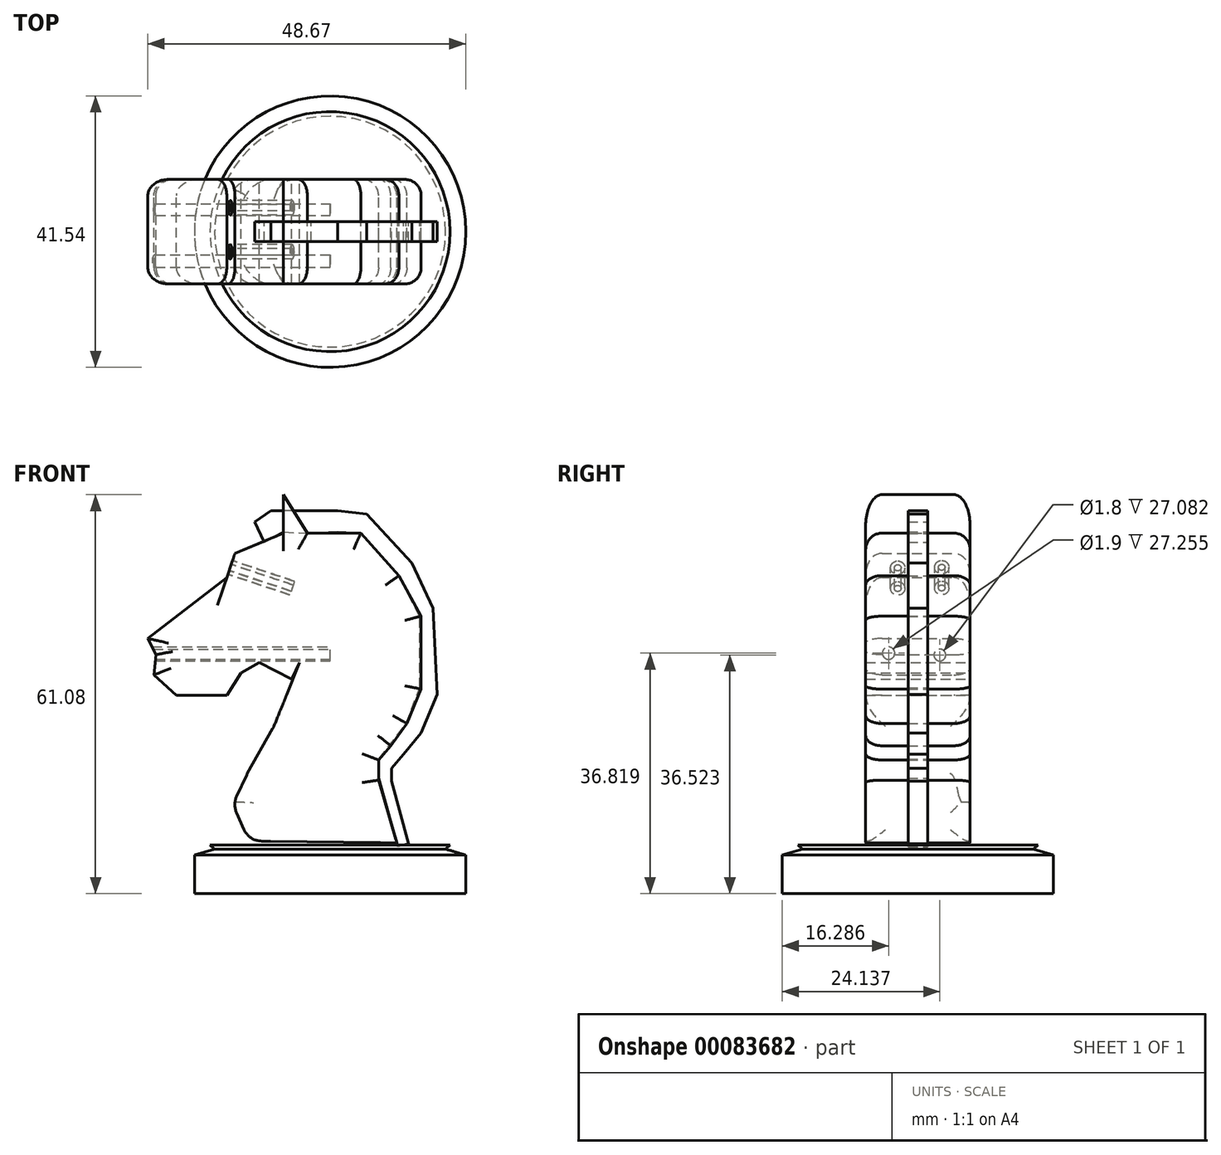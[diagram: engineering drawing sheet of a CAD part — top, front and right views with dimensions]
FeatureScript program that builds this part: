
annotation { "Feature Type Name" : "Feature", "Feature Type Description" : "" }
export const myFeature = defineFeature(function(context is Context, id is Id, definition is map)
    precondition{}
    {
        {
            var Q0;
            Q0=qCreatedBy(makeId("Front.planeOp"),FACE);
            var sketch = newSketch(context, id + "F0", { "sketchPlane" : qUnion([Q0])});
            skLineSegment(sketch, "E0", {"start": v(0, -48.68) * mm, "end": v(20.77, -48.68) * mm});
            skLineSegment(sketch, "E1", {"start": v(20.77, -48.68) * mm, "end": v(20.77, -42.79) * mm});
            skLineSegment(sketch, "E2", {"start": v(20.77, -42.79) * mm, "end": v(17.67, -41.86) * mm});
            skLineSegment(sketch, "E3", {"start": v(17.67, -41.86) * mm, "end": v(18.37, -41.27) * mm});
            skLineSegment(sketch, "E4", {"start": v(18.37, -41.27) * mm, "end": v(0, -41.27) * mm});
            skLineSegment(sketch, "E5", {"start": v(0, -41.27) * mm, "end": v(0, -48.68) * mm});
            skSolve(sketch);
        }
        {
            var Q0;
            Q0=makeQuery(id+"F0.imprint","IMPRINT",FACE,{"disambiguationData":[TD([[makeQuery(id+"F0.imprint","IMPRINT",EDGE,{"derivedFrom":sQuery(id+"F0.wireOp",EDGE,"E0")}),1.0]])]});
            var Q1;
            Q1=sQuery(id+"F0.wireOp",EDGE,"E5");
            revolve(context, id + "F1", {"entities" : qUnion([Q0]), "axis" : qUnion([Q1]), "revolveType" : RevolveType.FULL});
        }
        {
            var Q0;
            Q0=qCreatedBy(makeId("Front.planeOp"),FACE);
            var sketch = newSketch(context, id + "F2", { "sketchPlane" : qUnion([Q0])});
            skLineSegment(sketch, "E6", {"start": v(10.23, -40.93) * mm, "end": v(7.44, -31.31) * mm});
            skLineSegment(sketch, "E7", {"start": v(7.44, -31.31) * mm, "end": v(7.44, -28.21) * mm});
            skLineSegment(sketch, "E8", {"start": v(7.44, -28.21) * mm, "end": v(9.3, -26.04) * mm});
            skLineSegment(sketch, "E9", {"start": v(9.3, -26.04) * mm, "end": v(11.78, -22.63) * mm});
            skLineSegment(sketch, "E10", {"start": v(11.78, -22.63) * mm, "end": v(13.95, -17.36) * mm});
            skLineSegment(sketch, "E11", {"start": v(13.95, -17.36) * mm, "end": v(13.95, -12.4) * mm});
            skLineSegment(sketch, "E12", {"start": v(13.95, -12.4) * mm, "end": v(13.95, -6.2) * mm});
            skLineSegment(sketch, "E13", {"start": v(13.95, -6.2) * mm, "end": v(10.54, 0) * mm});
            skLineSegment(sketch, "E14", {"start": v(10.54, 0) * mm, "end": v(4.72, 6.51) * mm});
            skLineSegment(sketch, "E15", {"start": v(4.72, 6.51) * mm, "end": v(-3.48, 6.51) * mm});
            skLineSegment(sketch, "E16", {"start": v(-3.48, 6.51) * mm, "end": v(-7.13, 12.4) * mm});
            skLineSegment(sketch, "E17", {"start": v(-7.13, 12.4) * mm, "end": v(-7.13, 6.51) * mm});
            skLineSegment(sketch, "E18", {"start": v(-7.13, 6.51) * mm, "end": v(-14.57, 3.41) * mm});
            skLineSegment(sketch, "E19", {"start": v(-14.57, 3.41) * mm, "end": v(-15.81, -0.31) * mm});
            skLineSegment(sketch, "E20", {"start": v(-15.81, -0.31) * mm, "end": v(-27.9, -9.61) * mm});
            skLineSegment(sketch, "E21", {"start": v(-27.9, -9.61) * mm, "end": v(-26.66, -12.1) * mm});
            skLineSegment(sketch, "E22", {"start": v(-26.66, -12.1) * mm, "end": v(-26.97, -15.2) * mm});
            skLineSegment(sketch, "E23", {"start": v(-26.97, -15.2) * mm, "end": v(-23.56, -18.3) * mm});
            skLineSegment(sketch, "E24", {"start": v(-23.56, -18.3) * mm, "end": v(-15.81, -18.3) * mm});
            skLineSegment(sketch, "E25", {"start": v(-15.81, -18.3) * mm, "end": v(-13.64, -14.88) * mm});
            skLineSegment(sketch, "E26", {"start": v(-13.64, -14.88) * mm, "end": v(-10.85, -13.33) * mm});
            skLineSegment(sketch, "E27", {"start": v(-10.85, -13.33) * mm, "end": v(-5.9, -15.81) * mm});
            skLineSegment(sketch, "E28", {"start": v(-5.9, -15.81) * mm, "end": v(-4.65, -13.33) * mm});
            skLineSegment(sketch, "E29", {"start": v(-4.65, -13.33) * mm, "end": v(-8.68, -23.25) * mm});
            skLineSegment(sketch, "E30", {"start": v(-8.68, -23.25) * mm, "end": v(-12.71, -30.38) * mm});
            skLineSegment(sketch, "E31", {"start": v(-12.71, -30.38) * mm, "end": v(-14.88, -35.03) * mm});
            skLineSegment(sketch, "E32", {"start": v(-14.88, -35.03) * mm, "end": v(-12.4, -40.62) * mm});
            skLineSegment(sketch, "E33", {"start": v(-12.4, -40.62) * mm, "end": v(10.23, -40.93) * mm});
            skSolve(sketch);
        }
        {
            var Q0;
            Q0=makeQuery(id+"F2.imprint","IMPRINT",FACE,{"disambiguationData":[TD([[makeQuery(id+"F2.imprint","IMPRINT",EDGE,{"derivedFrom":sQuery(id+"F2.wireOp",EDGE,"E6")}),1.0]])]});
            extrude(context, id + "F3", {"entities" : qUnion([Q0]), "depth" : 8 * mm, "hasSecondDirection" : true, "secondDirectionOppositeDirection" : true, "secondDirectionDepth" : 8 * mm});
        }
        {
            var Q0;
            Q0=makeQuery(id+"F3.opExtrude","CAP_EDGE",EDGE,{"disambiguationData":[OSD([sQuery(id+"F2.wireOp",EDGE,"E20")])],"isStart":false});
            var Q1;
            Q1=makeQuery(id+"F3.opExtrude","CAP_EDGE",EDGE,{"disambiguationData":[OSD([sQuery(id+"F2.wireOp",EDGE,"E20")])],"isStart":true});
            var Q2;
            Q2=makeQuery(id+"F3.opExtrude","CAP_EDGE",EDGE,{"disambiguationData":[OSD([sQuery(id+"F2.wireOp",EDGE,"E21")])],"isStart":false});
            var Q3;
            Q3=makeQuery(id+"F3.opExtrude","CAP_EDGE",EDGE,{"disambiguationData":[OSD([sQuery(id+"F2.wireOp",EDGE,"E22")])],"isStart":false});
            var Q4;
            Q4=makeQuery(id+"F3.opExtrude","CAP_EDGE",EDGE,{"disambiguationData":[OSD([sQuery(id+"F2.wireOp",EDGE,"E23")])],"isStart":false});
            var Q5;
            Q5=makeQuery(id+"F3.opExtrude","CAP_EDGE",EDGE,{"disambiguationData":[OSD([sQuery(id+"F2.wireOp",EDGE,"E23")])],"isStart":true});
            var Q6;
            Q6=makeQuery(id+"F3.opExtrude","CAP_EDGE",EDGE,{"disambiguationData":[OSD([sQuery(id+"F2.wireOp",EDGE,"E22")])],"isStart":true});
            var Q7;
            Q7=makeQuery(id+"F3.opExtrude","CAP_EDGE",EDGE,{"disambiguationData":[OSD([sQuery(id+"F2.wireOp",EDGE,"E21")])],"isStart":true});
            var Q8;
            Q8=makeQuery(id+"F3.opExtrude","CAP_EDGE",EDGE,{"disambiguationData":[OSD([sQuery(id+"F2.wireOp",EDGE,"E15")])],"isStart":false});
            var Q9;
            Q9=makeQuery(id+"F3.opExtrude","CAP_EDGE",EDGE,{"disambiguationData":[OSD([sQuery(id+"F2.wireOp",EDGE,"E16")])],"isStart":false});
            var Q10;
            Q10=makeQuery(id+"F3.opExtrude","CAP_EDGE",EDGE,{"disambiguationData":[OSD([sQuery(id+"F2.wireOp",EDGE,"E14")])],"isStart":false});
            var Q11;
            Q11=makeQuery(id+"F3.opExtrude","CAP_EDGE",EDGE,{"disambiguationData":[OSD([sQuery(id+"F2.wireOp",EDGE,"E13")])],"isStart":false});
            var Q12;
            Q12=makeQuery(id+"F3.opExtrude","CAP_EDGE",EDGE,{"disambiguationData":[OSD([sQuery(id+"F2.wireOp",EDGE,"E11"),sQuery(id+"F2.wireOp",EDGE,"E12")])],"isStart":false});
            var Q13;
            Q13=makeQuery(id+"F3.opExtrude","CAP_EDGE",EDGE,{"disambiguationData":[OSD([sQuery(id+"F2.wireOp",EDGE,"E10")])],"isStart":false});
            var Q14;
            Q14=makeQuery(id+"F3.opExtrude","CAP_EDGE",EDGE,{"disambiguationData":[OSD([sQuery(id+"F2.wireOp",EDGE,"E9")])],"isStart":false});
            var Q15;
            Q15=makeQuery(id+"F3.opExtrude","CAP_EDGE",EDGE,{"disambiguationData":[OSD([sQuery(id+"F2.wireOp",EDGE,"E8")])],"isStart":false});
            var Q16;
            Q16=makeQuery(id+"F3.opExtrude","CAP_EDGE",EDGE,{"disambiguationData":[OSD([sQuery(id+"F2.wireOp",EDGE,"E7")])],"isStart":false});
            var Q17;
            Q17=makeQuery(id+"F3.opExtrude","CAP_EDGE",EDGE,{"disambiguationData":[OSD([sQuery(id+"F2.wireOp",EDGE,"E6")])],"isStart":false});
            var Q18;
            Q18=makeQuery(id+"F3.opExtrude","CAP_EDGE",EDGE,{"disambiguationData":[OSD([sQuery(id+"F2.wireOp",EDGE,"E6")])],"isStart":true});
            var Q19;
            Q19=makeQuery(id+"F3.opExtrude","CAP_EDGE",EDGE,{"disambiguationData":[OSD([sQuery(id+"F2.wireOp",EDGE,"E8")])],"isStart":true});
            var Q20;
            Q20=makeQuery(id+"F3.opExtrude","CAP_EDGE",EDGE,{"disambiguationData":[OSD([sQuery(id+"F2.wireOp",EDGE,"E10")])],"isStart":true});
            var Q21;
            Q21=makeQuery(id+"F3.opExtrude","CAP_EDGE",EDGE,{"disambiguationData":[OSD([sQuery(id+"F2.wireOp",EDGE,"E11"),sQuery(id+"F2.wireOp",EDGE,"E12")])],"isStart":true});
            var Q22;
            Q22=makeQuery(id+"F3.opExtrude","CAP_EDGE",EDGE,{"disambiguationData":[OSD([sQuery(id+"F2.wireOp",EDGE,"E13")])],"isStart":true});
            var Q23;
            Q23=makeQuery(id+"F3.opExtrude","CAP_EDGE",EDGE,{"disambiguationData":[OSD([sQuery(id+"F2.wireOp",EDGE,"E14")])],"isStart":true});
            var Q24;
            Q24=makeQuery(id+"F3.opExtrude","CAP_EDGE",EDGE,{"disambiguationData":[OSD([sQuery(id+"F2.wireOp",EDGE,"E15")])],"isStart":true});
            var Q25;
            Q25=makeQuery(id+"F3.opExtrude","CAP_EDGE",EDGE,{"disambiguationData":[OSD([sQuery(id+"F2.wireOp",EDGE,"E16")])],"isStart":true});
            var Q26;
            Q26=makeQuery(id+"F3.opExtrude","CAP_EDGE",EDGE,{"disambiguationData":[OSD([sQuery(id+"F2.wireOp",EDGE,"E9")])],"isStart":true});
            var Q27;
            Q27=makeQuery(id+"F3.opExtrude","CAP_EDGE",EDGE,{"disambiguationData":[OSD([sQuery(id+"F2.wireOp",EDGE,"E7")])],"isStart":true});
            var Q28;
            Q28=makeQuery(id+"F3.opExtrude","CAP_EDGE",EDGE,{"disambiguationData":[OSD([sQuery(id+"F2.wireOp",EDGE,"E18")])],"isStart":false});
            var Q29;
            Q29=makeQuery(id+"F3.opExtrude","CAP_EDGE",EDGE,{"disambiguationData":[OSD([sQuery(id+"F2.wireOp",EDGE,"E18")])],"isStart":true});
            fillet(context, id + "F4", {"entities" : qUnion([Q0, Q1, Q2, Q3, Q4, Q5, Q6, Q7, Q8, Q9, Q10, Q11, Q12, Q13, Q14, Q15, Q16, Q17, Q18, Q19, Q20, Q21, Q22, Q23, Q24, Q25, Q26, Q27, Q28, Q29]), "radius" : 2.5 * mm, "tangentPropagation" : true, "allowEdgeOverflow" : false});
        }
        {
            var Q0;
            Q0=makeQuery(id+"F3.opExtrude","CAP_EDGE",EDGE,{"disambiguationData":[OSD([sQuery(id+"F2.wireOp",EDGE,"E32")])],"isStart":true});
            var Q1;
            Q1=makeQuery(id+"F3.opExtrude","SWEPT_FACE",FACE,{"disambiguationData":[OSD([sQuery(id+"F2.wireOp",EDGE,"E30")])]});
            var Q2;
            Q2=makeQuery(id+"F3.opExtrude","CAP_EDGE",EDGE,{"disambiguationData":[OSD([sQuery(id+"F2.wireOp",EDGE,"E31")])],"isStart":false});
            var Q3;
            Q3=makeQuery(id+"F3.opExtrude","SWEPT_FACE",FACE,{"disambiguationData":[OSD([sQuery(id+"F2.wireOp",EDGE,"E32")])]});
            var Q4;
            Q4=makeQuery(id+"F3.opExtrude","SWEPT_EDGE",EDGE,{"disambiguationData":[OSD([sQuery(id+"F2.wireOp",EDGE,"E32"),sQuery(id+"F2.wireOp",EDGE,"E33")])]});
            var Q5;
            Q5=makeQuery(id+"F3.opExtrude","CAP_EDGE",EDGE,{"disambiguationData":[OSD([sQuery(id+"F2.wireOp",EDGE,"E32")])],"isStart":false});
            fillet(context, id + "F5", {"entities" : qUnion([Q0, Q1, Q2, Q3, Q4, Q5]), "radius" : 3 * mm, "tangentPropagation" : true, "allowEdgeOverflow" : false});
        }
        {
            var Q0;
            Q0=qCreatedBy(makeId("Right.planeOp"),FACE);
            var sketch = newSketch(context, id + "F6", { "sketchPlane" : qUnion([Q0])});
            skCircle(sketch, "E34", {"center": v(-4.48, -11.86) * mm, "radius": 0.95 * mm});
            skCircle(sketch, "E35", {"center": v(3.37, -12.16) * mm, "radius": 0.9 * mm});
            skSolve(sketch);
        }
        {
            var Q0;
            Q0 = qSketchRegion(id + "F6", true);
            var Q1;
            Q1=sQuery(id+"F6.wireOp",EDGE,"E35");
            var Q2;
            Q2=sQuery(id+"F6.wireOp",EDGE,"E34");
            extrude(context, id + "F7", {"entities" : qUnion([Q0]), "operationType" : NewBodyOperationType.REMOVE, "surfaceEntities" : qUnion([Q1, Q2]), "endBound" : BoundingType.THROUGH_ALL, "oppositeDirection" : true, "depth" : 25 * mm});
        }
        {
            var Q0;
            Q0=makeQuery(id+"F3.opExtrude","SWEPT_FACE",FACE,{"disambiguationData":[OSD([sQuery(id+"F2.wireOp",EDGE,"E19")])]});
            var sketch = newSketch(context, id + "F8", { "sketchPlane" : qUnion([Q0])});
            skCircle(sketch, "E36", {"center": v(3.09, -3.7) * mm, "radius": 1.1 * mm});
            skCircle(sketch, "E37", {"center": v(-3.65, -3.62) * mm, "radius": 1.1 * mm});
            skCircle(sketch, "E38", {"center": v(3.09, -3.7) * mm, "radius": 0.5 * mm});
            skCircle(sketch, "E39", {"center": v(-3.65, -3.62) * mm, "radius": 0.5 * mm});
            skSolve(sketch);
        }
        {
            var Q0;
            Q0=makeQuery(id+"F8.imprint","IMPRINT",FACE,{"disambiguationData":[TD([[makeQuery(id+"F8.imprint","IMPRINT",EDGE,{"derivedFrom":sQuery(id+"F8.wireOp",EDGE,"E37")}),1.0]])]});
            var Q1;
            Q1=makeQuery(id+"F8.imprint","IMPRINT",FACE,{"disambiguationData":[TD([[makeQuery(id+"F8.imprint","IMPRINT",EDGE,{"derivedFrom":sQuery(id+"F8.wireOp",EDGE,"E36")}),1.0]])]});
            var Q2;
            Q2=sQuery(id+"F8.wireOp",EDGE,"E37");
            var Q3;
            Q3=sQuery(id+"F8.wireOp",EDGE,"E36");
            extrude(context, id + "F9", {"entities" : qUnion([Q0, Q1]), "operationType" : NewBodyOperationType.REMOVE, "surfaceEntities" : qUnion([Q2, Q3]), "oppositeDirection" : true, "depth" : 10 * mm});
        }
        {
            var Q0;
            Q0=qCreatedBy(makeId("Front.planeOp"),FACE);
            var sketch = newSketch(context, id + "F10", { "sketchPlane" : qUnion([Q0])});
            skLineSegment(sketch, "E40", {"start": v(1.2, 6.62) * mm, "end": v(1.2, 9.92) * mm});
            skLineSegment(sketch, "E41", {"start": v(1.2, 9.92) * mm, "end": v(5.62, 9.44) * mm});
            skLineSegment(sketch, "E42", {"start": v(5.62, 9.44) * mm, "end": v(12.53, 1.96) * mm});
            skLineSegment(sketch, "E43", {"start": v(12.53, 1.96) * mm, "end": v(15.75, -4.95) * mm});
            skLineSegment(sketch, "E44", {"start": v(15.75, -4.95) * mm, "end": v(16.4, -18.22) * mm});
            skLineSegment(sketch, "E45", {"start": v(16.4, -18.22) * mm, "end": v(13.9, -24.09) * mm});
            skLineSegment(sketch, "E46", {"start": v(13.9, -24.09) * mm, "end": v(11.25, -27.3) * mm});
            skLineSegment(sketch, "E47", {"start": v(11.25, -27.3) * mm, "end": v(9.4, -29.47) * mm});
            skLineSegment(sketch, "E48", {"start": v(9.4, -29.47) * mm, "end": v(9.4, -31.48) * mm});
            skLineSegment(sketch, "E49", {"start": v(9.4, -31.48) * mm, "end": v(12.05, -41.05) * mm});
            skLineSegment(sketch, "E50", {"start": v(12.05, -41.05) * mm, "end": v(10.39, -41.51) * mm});
            skLineSegment(sketch, "E51", {"start": v(10.39, -41.51) * mm, "end": v(7.48, -31.01) * mm});
            skLineSegment(sketch, "E52", {"start": v(7.48, -31.01) * mm, "end": v(7.48, -28.1) * mm});
            skLineSegment(sketch, "E53", {"start": v(7.48, -28.1) * mm, "end": v(11.65, -22.64) * mm});
            skLineSegment(sketch, "E54", {"start": v(11.65, -22.64) * mm, "end": v(13.74, -17.17) * mm});
            skLineSegment(sketch, "E55", {"start": v(13.74, -17.17) * mm, "end": v(13.74, -6.24) * mm});
            skLineSegment(sketch, "E56", {"start": v(13.74, -6.24) * mm, "end": v(10.52, 0) * mm});
            skLineSegment(sketch, "E57", {"start": v(10.52, 0) * mm, "end": v(4.73, 6.46) * mm});
            skLineSegment(sketch, "E58", {"start": v(4.73, 6.46) * mm, "end": v(1.2, 6.62) * mm});
            skLineSegment(sketch, "E59", {"start": v(5.62, 9.44) * mm, "end": v(4.73, 6.46) * mm});
            skLineSegment(sketch, "E60", {"start": v(8.24, 6.6) * mm, "end": v(6.26, 4.76) * mm});
            skLineSegment(sketch, "E61", {"start": v(3.4, 9.68) * mm, "end": v(3.06, 6.54) * mm});
            skLineSegment(sketch, "E62", {"start": v(10.52, 4.13) * mm, "end": v(8.1, 1.96) * mm});
            skLineSegment(sketch, "E63", {"start": v(12.53, 1.96) * mm, "end": v(10.52, 0) * mm});
            skLineSegment(sketch, "E64", {"start": v(15.75, -4.95) * mm, "end": v(13.74, -6.24) * mm});
            skLineSegment(sketch, "E65", {"start": v(16.4, -18.22) * mm, "end": v(13.74, -17.17) * mm});
            skLineSegment(sketch, "E66", {"start": v(13.9, -24.09) * mm, "end": v(11.65, -22.64) * mm});
            skLineSegment(sketch, "E67", {"start": v(11.22, -27.43) * mm, "end": v(9.18, -25.87) * mm});
            skLineSegment(sketch, "E68", {"start": v(9.4, -29.47) * mm, "end": v(7.48, -28.1) * mm});
            skLineSegment(sketch, "E69", {"start": v(9.4, -31.48) * mm, "end": v(7.48, -31.01) * mm});
            skLineSegment(sketch, "E70", {"start": v(10.72, -36.26) * mm, "end": v(8.93, -36.76) * mm});
            skPoint(sketch, "E70.startSnap0", {"position": v(8.93, -36.26) * mm});
            skPoint(sketch, "E70.endSnap0", {"position": v(8.93, -36.26) * mm});
            skLineSegment(sketch, "E71", {"start": v(1.2, 9.92) * mm, "end": v(-2.9, 9.92) * mm});
            skLineSegment(sketch, "E72", {"start": v(-2.9, 9.92) * mm, "end": v(-2.9, 6.46) * mm});
            skLineSegment(sketch, "E73", {"start": v(-2.9, 6.46) * mm, "end": v(1.2, 6.62) * mm});
            skLineSegment(sketch, "E74", {"start": v(-2.9, 9.92) * mm, "end": v(-5.44, 9.92) * mm});
            skLineSegment(sketch, "E75", {"start": v(-5.44, 9.92) * mm, "end": v(-9.08, 9.92) * mm});
            skLineSegment(sketch, "E76", {"start": v(-9.08, 9.92) * mm, "end": v(-11.5, 8.23) * mm});
            skLineSegment(sketch, "E77", {"start": v(-11.5, 8.23) * mm, "end": v(-10.07, 5.14) * mm});
            skLineSegment(sketch, "E78", {"start": v(-10.07, 5.14) * mm, "end": v(-7.1, 6.68) * mm});
            skLineSegment(sketch, "E79", {"start": v(-7.1, 6.68) * mm, "end": v(-2.9, 6.46) * mm});
            skSolve(sketch);
        }
        {
            var Q0;
            Q0 = qSketchRegion(id + "F10", true);
            var Q1;
            Q1 = qConstructionFilter(qBodyType(qCreatedBy(id + "F10" ,EDGE), BodyType.WIRE), ConstructionObject.NO);
            extrude(context, id + "F11", {"entities" : qUnion([Q0]), "surfaceEntities" : qUnion([Q1]), "depth" : 1.5 * mm, "hasSecondDirection" : true, "secondDirectionOppositeDirection" : true, "secondDirectionDepth" : 1.5 * mm});
        }
    });
